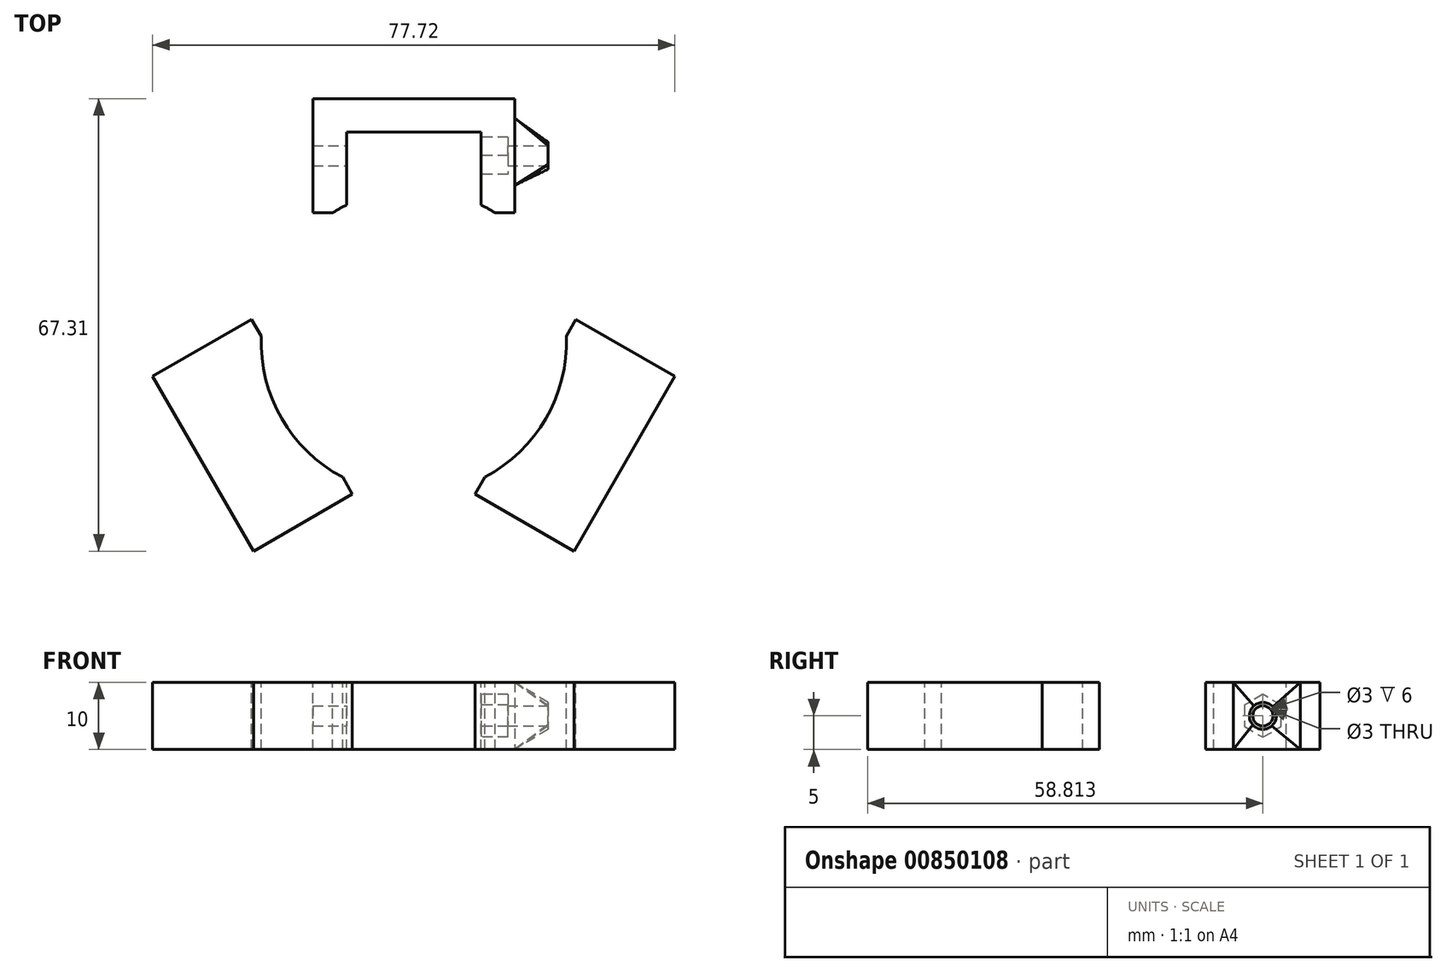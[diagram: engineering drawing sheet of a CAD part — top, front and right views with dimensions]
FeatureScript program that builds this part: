
annotation { "Feature Type Name" : "Feature", "Feature Type Description" : "" }
export const myFeature = defineFeature(function(context is Context, id is Id, definition is map)
    precondition{}
    {
        {
            var Q0;
            Q0=qCreatedBy(makeId("Top.planeOp"),FACE);
            var sketch = newSketch(context, id + "F0", { "sketchPlane" : qUnion([Q0])});
            skCircle(sketch, "E0.cCircle", {"center": v(0, 0) * mm, "radius": 27.71 * mm, "construction": true});
            skLineSegment(sketch, "E0.0", {"start": v(-16, 27.71) * mm, "end": v(16, 27.71) * mm, "construction": true});
            skLineSegment(sketch, "E0.1", {"start": v(16, 27.71) * mm, "end": v(32, 0) * mm, "construction": true});
            skLineSegment(sketch, "E0.2", {"start": v(32, 0) * mm, "end": v(16, -27.71) * mm, "construction": true});
            skLineSegment(sketch, "E0.3", {"start": v(16, -27.71) * mm, "end": v(-16, -27.71) * mm, "construction": true});
            skLineSegment(sketch, "E0.4", {"start": v(-16, -27.71) * mm, "end": v(-32, 0) * mm, "construction": true});
            skLineSegment(sketch, "E0.5", {"start": v(-32, 0) * mm, "end": v(-16, 27.71) * mm, "construction": true});
            skPoint(sketch, "E0.0.midPoint", {"position": v(0, 27.71) * mm});
            skLineSegment(sketch, "E1.bottom", {"start": v(15, 32.71) * mm, "end": v(-15, 32.71) * mm});
            skLineSegment(sketch, "E1.top", {"start": v(15, 22.71) * mm, "end": v(-15, 22.71) * mm});
            skLineSegment(sketch, "E1.left", {"start": v(15, 32.71) * mm, "end": v(15, 22.71) * mm});
            skLineSegment(sketch, "E1.right", {"start": v(-15, 32.71) * mm, "end": v(-15, 22.71) * mm});
            skLineSegment(sketch, "E2.bottom", {"start": v(-15, 36.21) * mm, "end": v(15, 36.21) * mm});
            skLineSegment(sketch, "E2.top", {"start": v(-15, 19.21) * mm, "end": v(15, 19.21) * mm});
            skLineSegment(sketch, "E2.left", {"start": v(-15, 36.21) * mm, "end": v(-15, 19.21) * mm});
            skLineSegment(sketch, "E2.right", {"start": v(15, 36.21) * mm, "end": v(15, 19.21) * mm});
            skLineSegment(sketch, "E3.1.0", {"start": v(-35.83, -3.37) * mm, "end": v(-20.83, -29.35) * mm});
            skLineSegment(sketch, "E3.1.1", {"start": v(-23.86, -31.1) * mm, "end": v(-38.86, -5.12) * mm});
            skLineSegment(sketch, "E3.1.2", {"start": v(-23.86, -31.1) * mm, "end": v(-9.14, -22.6) * mm});
            skLineSegment(sketch, "E3.1.3", {"start": v(-20.83, -29.35) * mm, "end": v(-12.17, -24.35) * mm});
            skLineSegment(sketch, "E3.1.4", {"start": v(-27.17, 1.63) * mm, "end": v(-12.17, -24.35) * mm});
            skLineSegment(sketch, "E3.1.5", {"start": v(-9.14, -22.6) * mm, "end": v(-24.14, 3.38) * mm});
            skLineSegment(sketch, "E3.1.6", {"start": v(-38.86, -5.12) * mm, "end": v(-24.14, 3.38) * mm});
            skLineSegment(sketch, "E3.1.7", {"start": v(-35.83, -3.37) * mm, "end": v(-27.17, 1.63) * mm});
            skLineSegment(sketch, "E3.2.0", {"start": v(20.83, -29.35) * mm, "end": v(35.83, -3.37) * mm});
            skLineSegment(sketch, "E3.2.1", {"start": v(38.86, -5.12) * mm, "end": v(23.86, -31.1) * mm});
            skLineSegment(sketch, "E3.2.2", {"start": v(38.86, -5.12) * mm, "end": v(24.14, 3.38) * mm});
            skLineSegment(sketch, "E3.2.3", {"start": v(35.83, -3.37) * mm, "end": v(27.17, 1.63) * mm});
            skLineSegment(sketch, "E3.2.4", {"start": v(12.17, -24.35) * mm, "end": v(27.17, 1.63) * mm});
            skLineSegment(sketch, "E3.2.5", {"start": v(24.14, 3.38) * mm, "end": v(9.14, -22.6) * mm});
            skLineSegment(sketch, "E3.2.6", {"start": v(23.86, -31.1) * mm, "end": v(9.14, -22.6) * mm});
            skLineSegment(sketch, "E3.2.7", {"start": v(20.83, -29.35) * mm, "end": v(12.17, -24.35) * mm});
            skCircle(sketch, "E4", {"center": v(0, 0) * mm, "radius": 27.71 * mm});
            skCircle(sketch, "E5", {"center": v(0, 0) * mm, "radius": 22.71 * mm});
            skSolve(sketch);
        }
        {
            var Q0;
            {var subQ0=sQuery(id+"F0.wireOp",EDGE,"E2.right");var subQ1=sQuery(id+"F0.wireOp",EDGE,"E1.top");var subQ2=makeQuery(id+"F0.imprint","INTERSECT",VERTEX,{"derivedFrom":[subQ1,subQ0]});Q0=makeQuery(id+"F0.imprint","IMPRINT",FACE,{"disambiguationData":[TD([[makeQuery(id+"F0.imprint","IMPRINT",EDGE,{"disambiguationData":[TD([[subQ2,-1.0]])],"derivedFrom":subQ1}),-1.0]])]});}
            var Q1;
            {var subQ0=sQuery(id+"F0.wireOp",EDGE,"E1.bottom");Q1=makeQuery(id+"F0.imprint","IMPRINT",FACE,{"disambiguationData":[TD([[makeQuery(id+"F0.imprint","IMPRINT",EDGE,{"derivedFrom":subQ0}),1.0]])]});}
            var Q2;
            {var subQ0=sQuery(id+"F0.wireOp",EDGE,"E1.bottom");Q2=makeQuery(id+"F0.imprint","IMPRINT",FACE,{"disambiguationData":[TD([[makeQuery(id+"F0.imprint","IMPRINT",EDGE,{"derivedFrom":subQ0}),-1.0]])]});}
            var Q3;
            {var subQ0=sQuery(id+"F0.wireOp",EDGE,"E3.2.0");Q3=makeQuery(id+"F0.imprint","IMPRINT",FACE,{"disambiguationData":[TD([[makeQuery(id+"F0.imprint","IMPRINT",EDGE,{"derivedFrom":subQ0}),1.0]])]});}
            var Q4;
            {var subQ0=sQuery(id+"F0.wireOp",EDGE,"E3.2.0");Q4=makeQuery(id+"F0.imprint","IMPRINT",FACE,{"disambiguationData":[TD([[makeQuery(id+"F0.imprint","IMPRINT",EDGE,{"derivedFrom":subQ0}),-1.0]])]});}
            var Q5;
            {var subQ0=sQuery(id+"F0.wireOp",EDGE,"E3.1.0");Q5=makeQuery(id+"F0.imprint","IMPRINT",FACE,{"disambiguationData":[TD([[makeQuery(id+"F0.imprint","IMPRINT",EDGE,{"derivedFrom":subQ0}),-1.0]])]});}
            var Q6;
            {var subQ3=sQuery(id+"F0.wireOp",EDGE,"E4");var subQ5=sQuery(id+"F0.wireOp",EDGE,"E3.1.3");var subQ8=makeQuery(id+"F0.imprint","INTERSECT",VERTEX,{"derivedFrom":[subQ5,subQ3]});Q6=makeQuery(id+"F0.imprint","IMPRINT",FACE,{"disambiguationData":[TD([[makeQuery(id+"F0.imprint","IMPRINT",EDGE,{"disambiguationData":[TD([[subQ8,1.0]])],"derivedFrom":subQ3}),1.0]])]});}
            var Q7;
            {var subQ0=sQuery(id+"F0.wireOp",EDGE,"E3.1.0");Q7=makeQuery(id+"F0.imprint","IMPRINT",FACE,{"disambiguationData":[TD([[makeQuery(id+"F0.imprint","IMPRINT",EDGE,{"derivedFrom":subQ0}),1.0]])]});}
            var Q8;
            {var subQ3=sQuery(id+"F0.wireOp",EDGE,"E4");var subQ5=sQuery(id+"F0.wireOp",EDGE,"E3.2.3");var subQ8=makeQuery(id+"F0.imprint","INTERSECT",VERTEX,{"derivedFrom":[subQ5,subQ3]});Q8=makeQuery(id+"F0.imprint","IMPRINT",FACE,{"disambiguationData":[TD([[makeQuery(id+"F0.imprint","IMPRINT",EDGE,{"disambiguationData":[TD([[subQ8,1.0]])],"derivedFrom":subQ3}),1.0]])]});}
            var Q9;
            {var subQ0=sQuery(id+"F0.wireOp",EDGE,"E2.left");var subQ1=sQuery(id+"F0.wireOp",EDGE,"E1.top");var subQ2=makeQuery(id+"F0.imprint","INTERSECT",VERTEX,{"derivedFrom":[subQ1,subQ0]});Q9=makeQuery(id+"F0.imprint","IMPRINT",FACE,{"disambiguationData":[TD([[makeQuery(id+"F0.imprint","IMPRINT",EDGE,{"disambiguationData":[TD([[subQ2,1.0]])],"derivedFrom":subQ1}),1.0]])]});}
            var Q10;
            {var subQ0=sQuery(id+"F0.wireOp",EDGE,"E2.right");var subQ1=sQuery(id+"F0.wireOp",EDGE,"E1.top");var subQ2=makeQuery(id+"F0.imprint","INTERSECT",VERTEX,{"derivedFrom":[subQ1,subQ0]});Q10=makeQuery(id+"F0.imprint","IMPRINT",FACE,{"disambiguationData":[TD([[makeQuery(id+"F0.imprint","IMPRINT",EDGE,{"disambiguationData":[TD([[subQ2,-1.0]])],"derivedFrom":subQ1}),1.0]])]});}
            var Q11;
            {var subQ5=sQuery(id+"F0.wireOp",EDGE,"E2.left");var subQ6=makeQuery(id+"F0.imprint","INTERSECT",VERTEX,{"derivedFrom":[sQuery(id+"F0.wireOp",EDGE,"E1.top"),subQ5]});Q11=makeQuery(id+"F0.imprint","IMPRINT",FACE,{"disambiguationData":[TD([[makeQuery(id+"F0.imprint","IMPRINT",EDGE,{"disambiguationData":[TD([[subQ6,1.0]])],"derivedFrom":subQ5}),-1.0]])]});}
            var Q12;
            {var subQ1=sQuery(id+"F0.wireOp",EDGE,"E3.1.4");var subQ3=sQuery(id+"F0.wireOp",EDGE,"E5");var subQ4=makeQuery(id+"F0.imprint","INTERSECT",VERTEX,{"derivedFrom":[subQ1,subQ3]});Q12=makeQuery(id+"F0.imprint","IMPRINT",FACE,{"disambiguationData":[TD([[makeQuery(id+"F0.imprint","IMPRINT",EDGE,{"disambiguationData":[TD([[subQ4,1.0]])],"derivedFrom":subQ3}),-1.0]])]});}
            var Q13;
            {var subQ1=sQuery(id+"F0.wireOp",EDGE,"E3.1.2");var subQ3=sQuery(id+"F0.wireOp",EDGE,"E5");var subQ4=makeQuery(id+"F0.imprint","INTERSECT",VERTEX,{"derivedFrom":[subQ1,subQ3]});Q13=makeQuery(id+"F0.imprint","IMPRINT",FACE,{"disambiguationData":[TD([[makeQuery(id+"F0.imprint","IMPRINT",EDGE,{"disambiguationData":[TD([[subQ4,1.0]])],"derivedFrom":subQ3}),-1.0]])]});}
            var Q14;
            {var subQ3=sQuery(id+"F0.wireOp",EDGE,"E4");var subQ7=sQuery(id+"F0.wireOp",EDGE,"E3.1.3");var subQ10=makeQuery(id+"F0.imprint","INTERSECT",VERTEX,{"derivedFrom":[subQ7,subQ3]});Q14=makeQuery(id+"F0.imprint","IMPRINT",FACE,{"disambiguationData":[TD([[makeQuery(id+"F0.imprint","IMPRINT",EDGE,{"disambiguationData":[TD([[subQ10,-1.0]])],"derivedFrom":subQ3}),1.0]])]});}
            var Q15;
            {var subQ1=sQuery(id+"F0.wireOp",EDGE,"E3.2.4");var subQ3=sQuery(id+"F0.wireOp",EDGE,"E5");var subQ4=makeQuery(id+"F0.imprint","INTERSECT",VERTEX,{"derivedFrom":[subQ1,subQ3]});Q15=makeQuery(id+"F0.imprint","IMPRINT",FACE,{"disambiguationData":[TD([[makeQuery(id+"F0.imprint","IMPRINT",EDGE,{"disambiguationData":[TD([[subQ4,1.0]])],"derivedFrom":subQ3}),-1.0]])]});}
            var Q16;
            {var subQ1=sQuery(id+"F0.wireOp",EDGE,"E3.2.2");var subQ3=sQuery(id+"F0.wireOp",EDGE,"E5");var subQ4=makeQuery(id+"F0.imprint","INTERSECT",VERTEX,{"derivedFrom":[subQ1,subQ3]});Q16=makeQuery(id+"F0.imprint","IMPRINT",FACE,{"disambiguationData":[TD([[makeQuery(id+"F0.imprint","IMPRINT",EDGE,{"disambiguationData":[TD([[subQ4,1.0]])],"derivedFrom":subQ3}),-1.0]])]});}
            var Q17;
            {var subQ7=sQuery(id+"F0.wireOp",EDGE,"E2.right");var subQ8=makeQuery(id+"F0.imprint","INTERSECT",VERTEX,{"derivedFrom":[sQuery(id+"F0.wireOp",EDGE,"E1.top"),subQ7]});Q17=makeQuery(id+"F0.imprint","IMPRINT",FACE,{"disambiguationData":[TD([[makeQuery(id+"F0.imprint","IMPRINT",EDGE,{"disambiguationData":[TD([[subQ8,1.0]])],"derivedFrom":subQ7}),1.0]])]});}
            extrude(context, id + "F1", {"entities" : qUnion([Q0, Q1, Q2, Q3, Q4, Q5, Q6, Q7, Q8, Q9, Q10, Q11, Q12, Q13, Q14, Q15, Q16, Q17]), "endBound" : BoundingType.SYMMETRIC, "oppositeDirection" : true, "depth" : 10 * mm, "offsetDistance" : 25 * mm});
        }
        {
            var Q0;
            Q0=makeQuery(id+"F1.opExtrude","SWEPT_FACE",FACE,{"disambiguationData":[OSD([sQuery(id+"F0.wireOp",EDGE,"E2.right")])]});
            cPlane(context, id + "F2", {"entities" : qUnion([Q0]), "cplaneType" : CPlaneType.OFFSET, "offset" : 5 * mm, "width" : 150 * mm, "height" : 150 * mm});
        }
        {
            var Q0;
            Q0=qCreatedBy(id+"F2.planeOp",FACE);
            var sketch = newSketch(context, id + "F3", { "sketchPlane" : qUnion([Q0])});
            skPoint(sketch, "E6.0", {"position": v(36.21, -5) * mm});
            skPoint(sketch, "E7.0", {"position": v(23.3, 5) * mm});
            skCircle(sketch, "E8", {"center": v(27.71, 0) * mm, "radius": 2 * mm});
            skSolve(sketch);
        }
        {
            var Q0;
            Q0=makeQuery(id+"F1.opExtrude","SWEPT_FACE",FACE,{"disambiguationData":[OSD([sQuery(id+"F0.wireOp",EDGE,"E2.right")])]});
            var sketch = newSketch(context, id + "F4", { "sketchPlane" : qUnion([Q0])});
            skLineSegment(sketch, "E9.bottom", {"start": v(23.3, 5) * mm, "end": v(33.3, 5) * mm});
            skLineSegment(sketch, "E9.top", {"start": v(23.3, -5) * mm, "end": v(33.3, -5) * mm});
            skLineSegment(sketch, "E9.left", {"start": v(23.3, 5) * mm, "end": v(23.3, -5) * mm});
            skLineSegment(sketch, "E9.right", {"start": v(33.3, 5) * mm, "end": v(33.3, -5) * mm});
            skSolve(sketch);
        }
        {
            var Q1;
            Q1=makeQuery(id+"F3.imprint","IMPRINT",FACE,{"disambiguationData":[TD([[makeQuery(id+"F3.imprint","IMPRINT",EDGE,{"derivedFrom":sQuery(id+"F3.wireOp",EDGE,"E8")}),1.0]])]});
            var Q2;
            Q2=makeQuery(id+"F4.imprint","IMPRINT",FACE,{"disambiguationData":[TD([[makeQuery(id+"F4.imprint","IMPRINT",EDGE,{"derivedFrom":sQuery(id+"F4.wireOp",EDGE,"E9.bottom")}),1.0]])]});
            loft(context, id + "F5", {"operationType" : NewBodyOperationType.ADD, "sheetProfilesArray" : [{ "sheetProfileEntities" : qUnion([Q1]) }, { "sheetProfileEntities" : qUnion([Q2]) }]});
        }
        {
            var Q0;
            Q0=makeQuery(id+"F5.opLoft","CAP_FACE",FACE,{"disambiguationData":[OSD([makeQuery(id+"F3.imprint","IMPRINT",FACE,{"disambiguationData":[TD([[makeQuery(id+"F3.imprint","IMPRINT",EDGE,{"derivedFrom":sQuery(id+"F3.wireOp",EDGE,"E8")}),1.0]])]})])],"isStart":true});
            var sketch = newSketch(context, id + "F6", { "sketchPlane" : qUnion([Q0])});
            skPoint(sketch, "E10.0", {"position": v(23.3, 5) * mm});
            skCircle(sketch, "E11", {"center": v(27.71, 0) * mm, "radius": 1.5 * mm});
            skSolve(sketch);
        }
        {
            var Q0;
            Q0 = qSketchRegion(id + "F6", true);
            extrude(context, id + "F7", {"entities" : qUnion([Q0]), "operationType" : NewBodyOperationType.REMOVE, "endBound" : BoundingType.THROUGH_ALL, "oppositeDirection" : true, "depth" : 25 * mm, "offsetDistance" : 25 * mm});
        }
        {
            var Q0;
            Q0=makeQuery(id+"F1.opExtrude","CAP_FACE",FACE,{"disambiguationData":[OSD([sQuery(id+"F0.wireOp",EDGE,"E2.bottom"),sQuery(id+"F0.wireOp",EDGE,"E2.left"),sQuery(id+"F0.wireOp",EDGE,"E2.right"),sQuery(id+"F0.wireOp",EDGE,"E3.1.1"),sQuery(id+"F0.wireOp",EDGE,"E3.1.2"),sQuery(id+"F0.wireOp",EDGE,"E3.1.3"),sQuery(id+"F0.wireOp",EDGE,"E3.1.6"),sQuery(id+"F0.wireOp",EDGE,"E3.1.7"),sQuery(id+"F0.wireOp",EDGE,"E3.2.1"),sQuery(id+"F0.wireOp",EDGE,"E3.2.2"),sQuery(id+"F0.wireOp",EDGE,"E3.2.3"),sQuery(id+"F0.wireOp",EDGE,"E3.2.6"),sQuery(id+"F0.wireOp",EDGE,"E3.2.7"),sQuery(id+"F0.wireOp",EDGE,"E4"),sQuery(id+"F0.wireOp",EDGE,"E5")])],"isStart":true});
            var sketch = newSketch(context, id + "F8", { "sketchPlane" : qUnion([Q0])});
            skLineSegment(sketch, "E12.bottom", {"start": v(-10, 31.21) * mm, "end": v(10, 31.21) * mm});
            skLineSegment(sketch, "E12.top", {"start": v(-10, 0) * mm, "end": v(10, 0) * mm});
            skLineSegment(sketch, "E12.left", {"start": v(-10, 31.21) * mm, "end": v(-10, 0) * mm});
            skLineSegment(sketch, "E12.right", {"start": v(10, 0) * mm, "end": v(10, 31.21) * mm});
            skSolve(sketch);
        }
        {
            var Q0;
            {var subQ0=sQuery(id+"F8.wireOp",EDGE,"E12.bottom");Q0=makeQuery(id+"F8.imprint","IMPRINT",FACE,{"disambiguationData":[TD([[makeQuery(id+"F8.imprint","IMPRINT",EDGE,{"derivedFrom":subQ0}),-1.0]])]});}
            extrude(context, id + "F9", {"entities" : qUnion([Q0]), "operationType" : NewBodyOperationType.REMOVE, "endBound" : BoundingType.THROUGH_ALL, "oppositeDirection" : true, "depth" : 25 * mm, "offsetDistance" : 25 * mm});
        }
        {
            var Q0;
            Q0=makeQuery(id+"F9.boolean.opBoolean","COPY",FACE,{"derivedFrom":makeQuery(id+"F9.opExtrude","SWEPT_FACE",FACE,{"disambiguationData":[OSD([sQuery(id+"F8.wireOp",EDGE,"E12.right")])]})});
            var sketch = newSketch(context, id + "F10", { "sketchPlane" : qUnion([Q0])});
            skCircle(sketch, "E13.cCircle", {"center": v(-27.71, 0) * mm, "radius": 2.75 * mm, "construction": true});
            skLineSegment(sketch, "E13.0", {"start": v(-27.71, 3.18) * mm, "end": v(-24.96, 1.59) * mm});
            skLineSegment(sketch, "E13.1", {"start": v(-24.96, 1.59) * mm, "end": v(-24.96, -1.59) * mm});
            skLineSegment(sketch, "E13.2", {"start": v(-24.96, -1.59) * mm, "end": v(-27.71, -3.18) * mm});
            skLineSegment(sketch, "E13.3", {"start": v(-27.71, -3.18) * mm, "end": v(-30.46, -1.59) * mm});
            skLineSegment(sketch, "E13.4", {"start": v(-30.46, -1.59) * mm, "end": v(-30.46, 1.59) * mm});
            skLineSegment(sketch, "E13.5", {"start": v(-30.46, 1.59) * mm, "end": v(-27.71, 3.18) * mm});
            skPoint(sketch, "E13.0.midPoint", {"position": v(-26.34, 2.38) * mm});
            skSolve(sketch);
        }
        {
            var Q0;
            Q0 = qSketchRegion(id + "F10", true);
            extrude(context, id + "F11", {"entities" : qUnion([Q0]), "operationType" : NewBodyOperationType.REMOVE, "oppositeDirection" : true, "depth" : 4 * mm, "offsetDistance" : 25 * mm});
        }
    });
